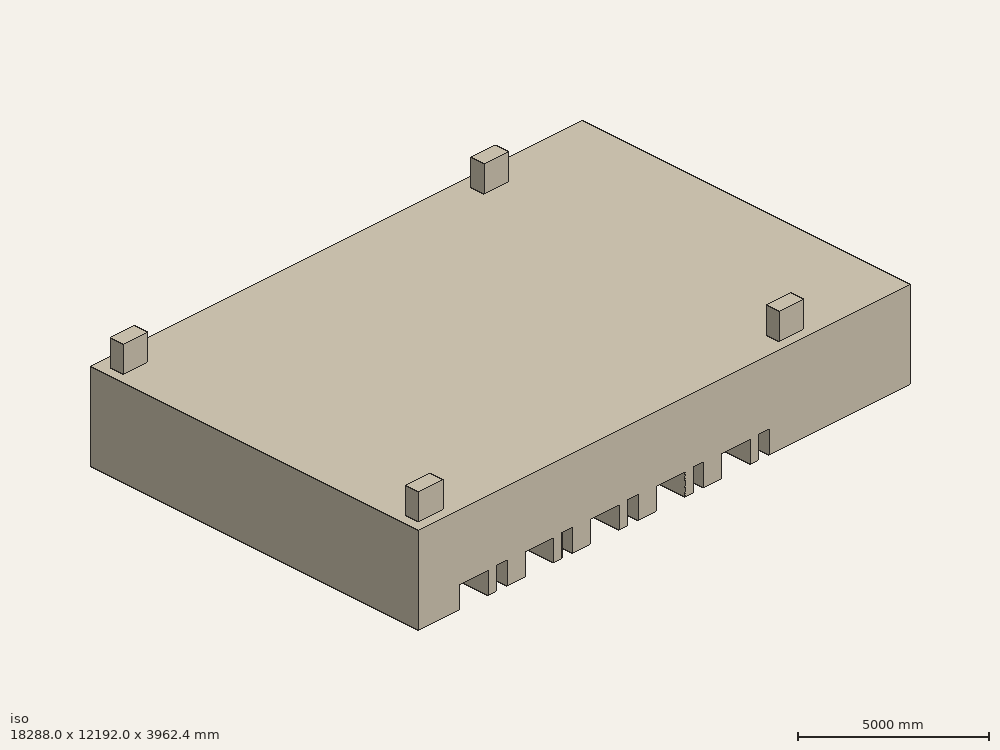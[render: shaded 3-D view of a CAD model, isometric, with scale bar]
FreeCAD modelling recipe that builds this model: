
FCSTD DOCUMENT  (FreeCAD 0.18R14555 (Git shallow))
Label: flow_domain
License: All rights reserved
LicenseURL: http://en.wikipedia.org/wiki/All_rights_reserved
objects: Part::Box×16, Part::MultiFuse×10, Part::Mirroring×1, Part::FeaturePython×1
note: 28 computed .brp shape members not serialized (recipe doc carries the construction recipe); baked Part::Feature solids carry a one-line shape summary decoded from their .brp

FEATURE [Part::Box] Box  label="Room"
  AttacherType = Attacher::AttachEngine3D
  Height = 3048
  Length = 18288
  Width = 12192
FEATURE [Part::Box] Box001  label="Bed 1"
  AttacherType = Attacher::AttachEngine3D
  Height = 762
  Length = 1066.8
  Width = 1981.2
FEATURE [Part::Box] Box002  label="Table 1"
  AttacherType = Attacher::AttachEngine3D
  Height = 798.576
  Length = 396.24
  Placement = pos=(1371.6,0,0) rot=(0,0,1;0rad)
  Width = 396.24
FEATURE [Part::MultiFuse] Fusion  label="Set 1"
  Shapes = -> [Box002,Box001]
FEATURE [Part::Box] Box003  label="Bed 002"
  AttacherType = Attacher::AttachEngine3D
  Height = 762
  Length = 1066.8
  Width = 1981.2
FEATURE [Part::Box] Box004  label="Table 002"
  AttacherType = Attacher::AttachEngine3D
  Height = 798.576
  Length = 396.24
  Placement = pos=(1371.6,0,0) rot=(0,0,1;0rad)
  Width = 396.24
FEATURE [Part::MultiFuse] Fusion001  label="Set 2"
  Placement = pos=(2438.4,0,0) rot=(0,0,1;0rad)
  Shapes = -> [Box004,Box003]
FEATURE [Part::Box] Box005  label="Table 003"
  AttacherType = Attacher::AttachEngine3D
  Height = 798.576
  Length = 396.24
  Placement = pos=(1371.6,0,0) rot=(0,0,1;0rad)
  Width = 396.24
FEATURE [Part::Box] Box006  label="Bed 003"
  AttacherType = Attacher::AttachEngine3D
  Height = 762
  Length = 1066.8
  Width = 1981.2
FEATURE [Part::MultiFuse] Fusion002  label="Set 3"
  Placement = pos=(4876.8,0,0) rot=(0,0,1;0rad)
  Shapes = -> [Box005,Box006]
FEATURE [Part::Box] Box007  label="Bed 004"
  AttacherType = Attacher::AttachEngine3D
  Height = 762
  Length = 1066.8
  Width = 1981.2
FEATURE [Part::Box] Box008  label="Table 004"
  AttacherType = Attacher::AttachEngine3D
  Height = 798.576
  Length = 396.24
  Placement = pos=(1371.6,0,0) rot=(0,0,1;0rad)
  Width = 396.24
FEATURE [Part::MultiFuse] Fusion003  label="Set 4"
  Placement = pos=(7315.2,0,0) rot=(0,0,1;0rad)
  Shapes = -> [Box008,Box007]
FEATURE [Part::Box] Box009  label="Table 005"
  AttacherType = Attacher::AttachEngine3D
  Height = 798.576
  Length = 396.24
  Placement = pos=(1371.6,0,0) rot=(0,0,1;0rad)
  Width = 396.24
FEATURE [Part::Box] Box010  label="Bed 005"
  AttacherType = Attacher::AttachEngine3D
  Height = 762
  Length = 1066.8
  Width = 1981.2
FEATURE [Part::MultiFuse] Fusion004  label="Set 5"
  Placement = pos=(9753.6,0,0) rot=(0,0,1;0rad)
  Shapes = -> [Box009,Box010]
FEATURE [Part::MultiFuse] Fusion005  label="right beds"
  Shapes = -> [Fusion001,Fusion002,Fusion003,Fusion004,Fusion]
FEATURE [Part::Mirroring] Part__Mirroring  label="left beds"
  Base = (0,6096,0)
  Normal = (0,1,0)
  Source = -> Fusion005
FEATURE [Part::Box] Box011  label="Nurse Station"
  AttacherType = Attacher::AttachEngine3D
  Height = 1219.2
  Length = 3048
  Placement = pos=(15240,7620,0) rot=(0,0,1;0rad)
  Width = 4572
FEATURE [Part::Box] Box014  label="Inlet 1"
  AttacherType = Attacher::AttachEngine3D
  Height = 1219.2
  Length = 914.4
  Placement = pos=(13716,11277.6,2743.2) rot=(0,0,1;0rad)
  Width = 487.68
FEATURE [Part::Box] Box015  label="Inlet 2"
  AttacherType = Attacher::AttachEngine3D
  Height = 1219.2
  Length = 914.4
  Placement = pos=(13716,304.8,2743.2) rot=(0,0,1;0rad)
  Width = 487.68
FEATURE [Part::Box] Box018  label="Outlet 2"
  AttacherType = Attacher::AttachEngine3D
  Height = 1219.2
  Length = 914.4
  Placement = pos=(304.8,304.8,2743.2) rot=(0,0,1;0rad)
  Width = 487.68
FEATURE [Part::Box] Box019  label="Outlet 1"
  AttacherType = Attacher::AttachEngine3D
  Height = 1219.2
  Length = 914.4
  Placement = pos=(304.8,11277.6,2743.2) rot=(0,0,1;0rad)
  Width = 487.68
FEATURE [Part::MultiFuse] Fusion006  label="all beds"
  Placement = pos=(1524,0,0) rot=(0,0,1;0rad)
  Shapes = -> [Part__Mirroring,Fusion005]
FEATURE [Part::MultiFuse] Fusion007  label="vents"
  Shapes = -> [Box014,Box015,Box018,Box019]
FEATURE [Part::MultiFuse] Fusion008  label="surfaces"
  Shapes = -> [Box011,Fusion006]
FEATURE [Part::MultiFuse] Fusion009
  Shapes = -> [Box,Fusion007]
FEATURE [Part::FeaturePython] XOR  label="flow_field"  # WARN: FeaturePython — macro-defined, semantics opaque (R4)
  Objects = -> [Fusion009,Fusion008]
  Tolerance = 0
